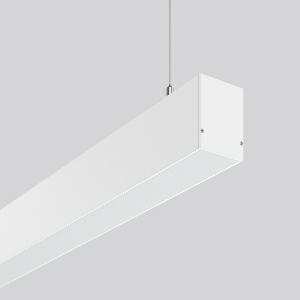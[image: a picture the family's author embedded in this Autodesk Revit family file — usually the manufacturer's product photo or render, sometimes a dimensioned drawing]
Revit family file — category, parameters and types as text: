
# Revit family: less_is_more_50_312317_002_1_9efc
name_source: partatom
category: Lighting Fixtures
units: mm (PartAtom-declared; Revit-internal decimal feet)

## family parameters
Cut with Voids When Loaded = No
Host = Face
Light Source = No
Part Type = Normal
Room Calculation Point = No
Round Connector Dimension = Use Diameter
Shared = No

## types (1)
- LESS IS MORE 50 (1 x LED Modul 840, 4000 lm, 4000)
    Apparent Load = 34 VA
    CIE Flux Codes = 49 80 96 63 100
    Color Rendering = 80
    Color Temperature = 4000
    Default Elevation = 1800 mm
    Description = Series: LESS IS MORE 50
Linear pendant luminaire for aesthetically sophisticated lighting. Housing: extruded aluminium profile, powder-coated. End cap aluminium powder-coated. Canopy made of aluminium, powder-coated. Diffuser made of non-yellowing plastic (PMMA), opal. Direct 65%, indirect 35% light emission. Suitable for pendant. 2-point steel cable suspension freely positionable and infinitely height-adjustable. Special lengths available on request. LED unit with integrated converter interchangeable and removable. Suitable for through-wiring. With sensors or as a safety luminaire on request. 
Colour: traffic white, matt (RAL 9016)
Length: 847 mm
Width: 57 mm
Height: 75 mm
Suspension length: 2000 mm
Lamp: LED
Socket: without socket
Colour temperature: 4000K
Colour rendering index (CRI): 80
Light source: LED
Socket lamp2: Without base
Colour temperature: 4000K
System power: 34 W
Rated luminous flux: 4000 lm
Luminous efficiency: 118 lm/W
Control gear: Regulated power supply
Control gear: Regulated power supply
Protection class: I
Type of protection: IP 20
    Height = 75 mm
    Lamp = 1 x LED Modul 840
    Lamp Light Flux = 4000 lm
    Lamp count = 1
    Length = 847 mm
    Lifetime = 50000 h
    Luminous efficacy = 118 lm/W
    Manufacturer = RZB
    ModVariant = No
    Model = 312317.002.1
    Mounting Place = Ceiling
    Mounting Type = Pendant
    Number of Poles = 1
    OnlyDefault = Yes
    Power Factor = 1
    Product Name = LESS IS MORE 50
    Product group = Pendant LED linear luminaires
    ProductGroupID = 907
    Protection Class = Protection class I
    Protection Degree = IP 20
    RLX_Detail_Level = 1
    RLX_Emergency_Light_Flux = 0 lm
    RLX_Emergency_Type = 0
    RLX_Emergency_Type_DB = No
    RlxData = <blob elided: 31625 chars, md5=e699024b>
    Socket = socket
    Standby Power = 0 W
    System Light Flux = 4000 lm
    System Power = 34 W
    Type Comments = Product without accessories
    Type Image = 312318.002.jpg
    URL = http://relux.com
    VarID = ---
    Voltage = 230 V
    Voltage Range = 220-240 V
    Weight = 0.00 kg
    Width = 57 mm

## geometry (parser evidence)
native form markers: Blend x4, Sweep x14
no freeform markers — native parametric forms only
